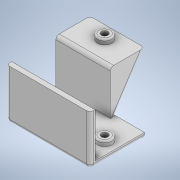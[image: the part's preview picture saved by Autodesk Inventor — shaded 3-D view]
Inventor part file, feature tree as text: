
AUTODESK INVENTOR PART (.ipt)
format: ipt  version: 2020 (Build 240168000, 168)  size: 280,064 bytes
history: native  units: in
note: dims shown in document units (in); Inventor stores cm internally (conversion verified against a paired STEP export)
features: extrude x14, sketch x14, fillet x3, mirror x1
ambient origin geometry x8: Origin, YZ Plane, XZ Plane, XY Plane, X Axis, Y Axis, Z Axis, Center Point
bodies: Solid1 (feature_tree)
feature tree (32):
  extrude  "Extrusion1"  Depth=1.2756in
  extrude  "Extrusion4"  Depth=0.1181in
  extrude  "Extrusion5"  Depth=0.1181in
  extrude  "Extrusion6"  Depth=0.1181in
  extrude  "Extrusion7"  Depth=0.1181in TaperAngle=0.0deg
  extrude  "Extrusion8"  Depth=0.1575in
  extrude  "Extrusion15"  Depth=0.2362in
  extrude  "Extrusion23"  Depth=0.1181in TaperAngle=0.0deg
  extrude  "Extrusion24"  Depth=1.2756in
  extrude  "Extrusion25"  Depth=1.0394in TaperAngle=0.0deg
  extrude  "Extrusion26"  Depth=0.1181in
  extrude  "Extrusion27"  Depth=0.6811in TaperAngle=0.0deg
  extrude  "Extrusion28"  Depth=1.2756in
  fillet  "Fillet3"  Radius=1.2756in
  fillet  "Fillet4"  Radius=0.3346in
  extrude  "Extrusion29"  Depth=0.1181in
  mirror  "Mirror2"
  fillet  "Fillet5"  Radius=1.0394in
  sketch  "Sketch1"  dims[d0=1.6142in d1=1.2756in]
  sketch  "Sketch4"  dims[d2=0.1181in d3=0.0in d12=0.8465in]
  sketch  "Sketch5"  dims[d13=0.1181in d14=0.0in d15=0.8465in]
  sketch  "Sketch6"  dims[d16=0.1181in d17=0.0in d20=0.3346in]
  sketch  "Sketch7"  dims[d21=0.3346in d22=0.1181in d23=0.0in]
  sketch  "Sketch8"  dims[d24=0.1575in d25=0.1575in]
  sketch  "Sketch15"  dims[d26=0.2362in d27=0.0in d28=0.2362in]
  sketch  "Sketch23"  dims[d29=0.2362in d30=0.1181in d31=0.0in]
  sketch  "Sketch24"  dims[d54=0.3425in d55=0.0in d81=1.2756in]
  sketch  "Sketch25"  dims[d82=0.1181in d83=1.0394in d84=0.0in]
  sketch  "Sketch26"  dims[d85=0.1181in d86=0.1181in]
  sketch  "Sketch27"  dims[d87=0.1181in d88=0.6811in d89=0.0in]
  sketch  "Sketch28"  dims[d90=1.2756in d91=0.0in d92=0.1575in d93=1.2756in d94=0.0in d95=0.3346in]
  sketch  "Sketch29"  dims[d96=0.1181in d97=0.0in d98=0.1181in d99=1.0394in d100=0.0in d101=0.0394in d102=0.0787in d103=0.2362in d104=0.1181in d105=0.0in d106=0.0787in d10=0.0197in d11=0.0344in d65=0.0197in d66=0.0344in d67=0.0197in d68=0.0344in]
